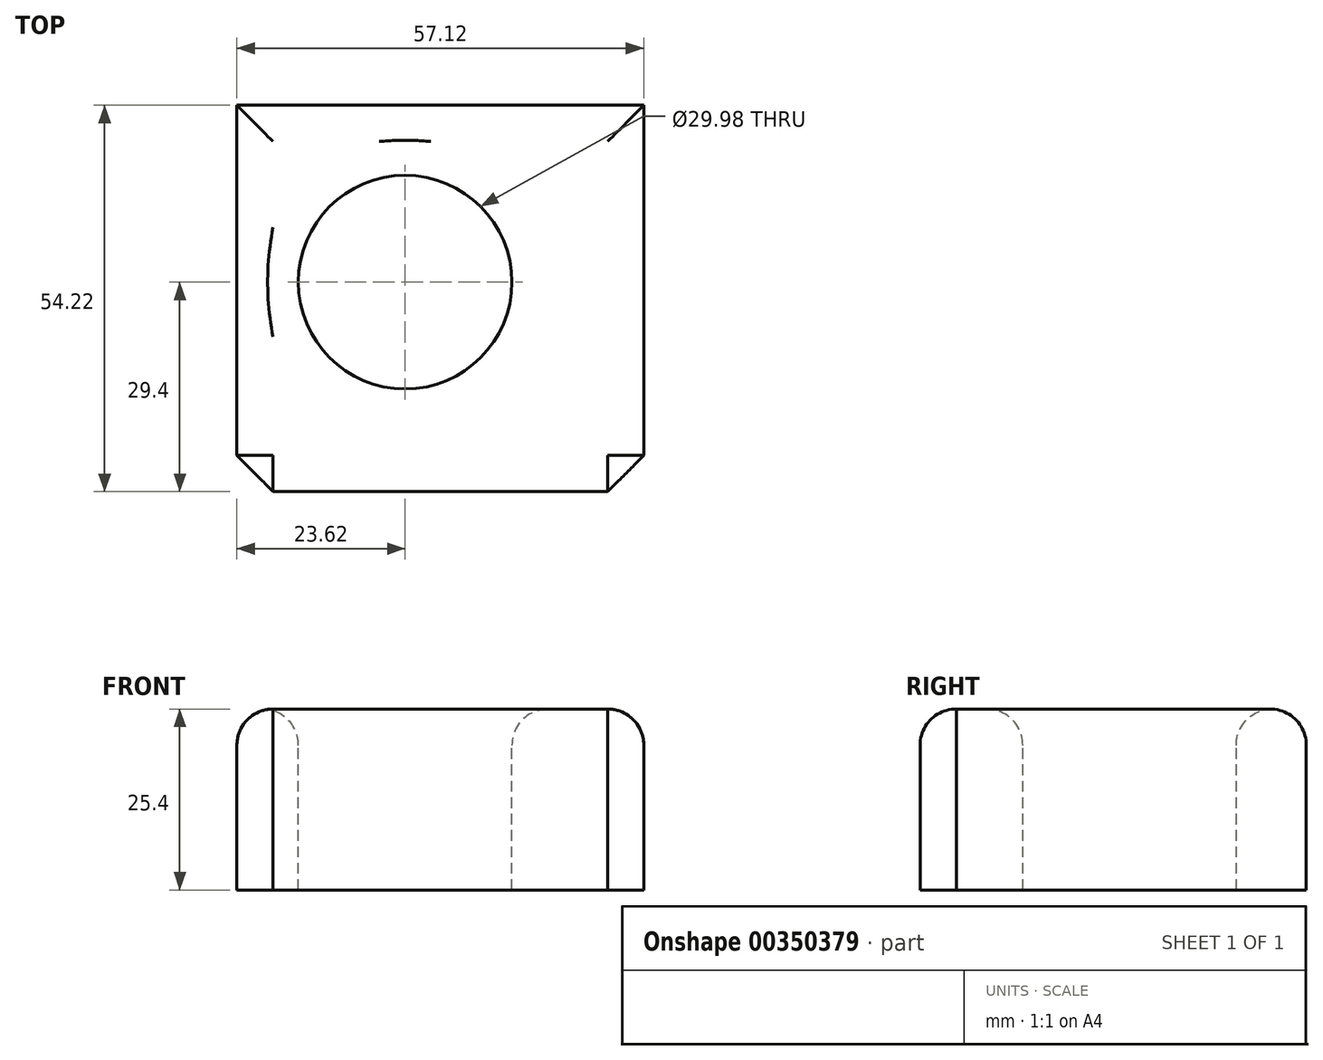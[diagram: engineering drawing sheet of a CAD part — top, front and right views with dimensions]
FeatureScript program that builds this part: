
annotation { "Feature Type Name" : "Feature", "Feature Type Description" : "" }
export const myFeature = defineFeature(function(context is Context, id is Id, definition is map)
    precondition{}
    {
        {
            var Q0;
            Q0=qCreatedBy(makeId("Top.planeOp"),FACE);
            var sketch = newSketch(context, id + "F0", { "sketchPlane" : qUnion([Q0])});
            skLineSegment(sketch, "E0.bottom", {"start": v(-23.62, 24.82) * mm, "end": v(33.5, 24.82) * mm});
            skLineSegment(sketch, "E0.top", {"start": v(-23.62, -29.4) * mm, "end": v(33.5, -29.4) * mm});
            skLineSegment(sketch, "E0.left", {"start": v(-23.62, 24.82) * mm, "end": v(-23.62, -29.4) * mm});
            skLineSegment(sketch, "E0.right", {"start": v(33.5, 24.82) * mm, "end": v(33.5, -29.4) * mm});
            skSolve(sketch);
        }
        {
            var Q0;
            Q0=makeQuery(id+"F0.imprint","IMPRINT",FACE,{"disambiguationData":[TD([[makeQuery(id+"F0.imprint","IMPRINT",EDGE,{"derivedFrom":sQuery(id+"F0.wireOp",EDGE,"E0.bottom")}),-1.0]])]});
            extrude(context, id + "F1", {"entities" : qUnion([Q0]), "depth" : 25.4 * mm});
        }
        {
            var Q0;
            Q0=makeQuery(id+"F1.opExtrude","CAP_FACE",FACE,{"disambiguationData":[OSD([sQuery(id+"F0.wireOp",EDGE,"E0.bottom"),sQuery(id+"F0.wireOp",EDGE,"E0.top"),sQuery(id+"F0.wireOp",EDGE,"E0.left"),sQuery(id+"F0.wireOp",EDGE,"E0.right")])],"isStart":false});
            var sketch = newSketch(context, id + "F2", { "sketchPlane" : qUnion([Q0])});
            skCircle(sketch, "E1", {"center": v(0, 0) * mm, "radius": 15 * mm});
            skSolve(sketch);
        }
        {
            var Q0;
            Q0=makeQuery(id+"F2.imprint","IMPRINT",FACE,{"disambiguationData":[TD([[makeQuery(id+"F2.imprint","IMPRINT",EDGE,{"derivedFrom":sQuery(id+"F2.wireOp",EDGE,"E1")}),1.0]])]});
            extrude(context, id + "F3", {"entities" : qUnion([Q0]), "operationType" : NewBodyOperationType.REMOVE, "oppositeDirection" : true, "depth" : 25.4 * mm});
        }
        {
            var Q0;
            Q0=makeQuery(id+"F1.opExtrude","CAP_FACE",FACE,{"disambiguationData":[OSD([sQuery(id+"F0.wireOp",EDGE,"E0.bottom"),sQuery(id+"F0.wireOp",EDGE,"E0.top"),sQuery(id+"F0.wireOp",EDGE,"E0.left"),sQuery(id+"F0.wireOp",EDGE,"E0.right")])],"isStart":false});
            fillet(context, id + "F4", {"entities" : qUnion([Q0]), "radius" : 5.08 * mm, "tangentPropagation" : true, "allowEdgeOverflow" : false});
        }
        {
            var Q0;
            Q0=makeQuery(id+"F1.opExtrude","SWEPT_EDGE",EDGE,{"disambiguationData":[OSD([sQuery(id+"F0.wireOp",EDGE,"E0.top"),sQuery(id+"F0.wireOp",EDGE,"E0.right")])]});
            var Q1;
            Q1=makeQuery(id+"F1.opExtrude","SWEPT_EDGE",EDGE,{"disambiguationData":[OSD([sQuery(id+"F0.wireOp",EDGE,"E0.top"),sQuery(id+"F0.wireOp",EDGE,"E0.left")])]});
            chamfer(context, id + "F5", {"entities" : qUnion([Q0, Q1]), "width" : 5.08 * mm, "tangentPropagation" : true});
        }
    });
